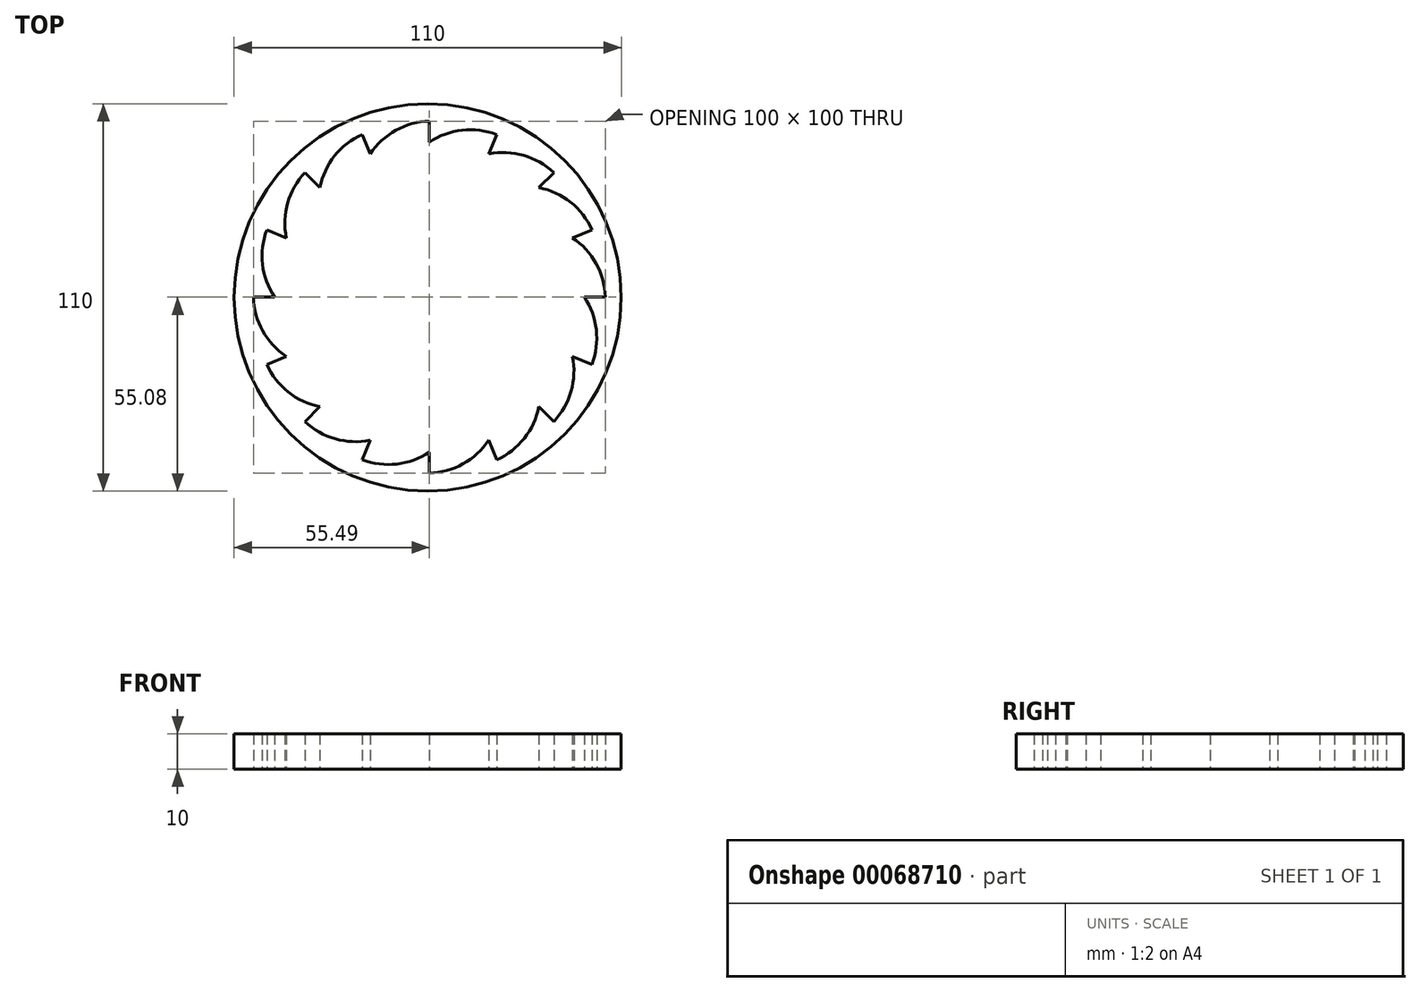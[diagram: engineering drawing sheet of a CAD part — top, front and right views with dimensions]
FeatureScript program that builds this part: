
annotation { "Feature Type Name" : "Feature", "Feature Type Description" : "" }
export const myFeature = defineFeature(function(context is Context, id is Id, definition is map)
    precondition{}
    {
        {
            var Q0;
            Q0=qCreatedBy(makeId("Top.planeOp"),FACE);
            var sketch = newSketch(context, id + "F0", { "sketchPlane" : qUnion([Q0])});
            skLineSegment(sketch, "E0", {"start": v(0, 44) * mm, "end": v(0, 50) * mm});
            skLineSegment(sketch, "E1", {"start": v(16.84, 40.65) * mm, "end": v(19.13, 46.2) * mm});
            skLineSegment(sketch, "E2", {"start": v(35.36, 35.36) * mm, "end": v(31.11, 31.11) * mm});
            skLineSegment(sketch, "E3", {"start": v(40.65, 16.84) * mm, "end": v(46.2, 19.13) * mm});
            skArc(sketch, "E4", {"start": v(19.13, 46.2) * mm, "mid": v(9.3, 47.42) * mm, "end": v(0, 44) * mm});
            skArc(sketch, "E5", {"start": v(35.36, 35.36) * mm, "mid": v(26.74, 40.25) * mm, "end": v(16.84, 40.65) * mm});
            skArc(sketch, "E6", {"start": v(46.2, 19.13) * mm, "mid": v(40.1, 26.95) * mm, "end": v(31.11, 31.11) * mm});
            skArc(sketch, "E7", {"start": v(50, 0) * mm, "mid": v(47.37, 9.55) * mm, "end": v(40.65, 16.84) * mm});
            skLineSegment(sketch, "E8.1.0", {"start": v(-44, 0) * mm, "end": v(-50, 0) * mm});
            skArc(sketch, "E8.1.1", {"start": v(-46.2, 19.13) * mm, "mid": v(-47.42, 9.3) * mm, "end": v(-44, 0) * mm});
            skLineSegment(sketch, "E8.1.2", {"start": v(-40.65, 16.84) * mm, "end": v(-46.2, 19.13) * mm});
            skArc(sketch, "E8.1.3", {"start": v(-35.36, 35.36) * mm, "mid": v(-40.25, 26.74) * mm, "end": v(-40.65, 16.84) * mm});
            skLineSegment(sketch, "E8.1.4", {"start": v(-35.36, 35.36) * mm, "end": v(-31.11, 31.11) * mm});
            skArc(sketch, "E8.1.5", {"start": v(-19.13, 46.2) * mm, "mid": v(-26.95, 40.1) * mm, "end": v(-31.11, 31.11) * mm});
            skArc(sketch, "E8.1.6", {"start": v(0, 50) * mm, "mid": v(-9.55, 47.37) * mm, "end": v(-16.84, 40.65) * mm});
            skLineSegment(sketch, "E8.1.7", {"start": v(-16.84, 40.65) * mm, "end": v(-19.13, 46.2) * mm});
            skLineSegment(sketch, "E8.2.0", {"start": v(0, -44) * mm, "end": v(0, -50) * mm});
            skArc(sketch, "E8.2.1", {"start": v(-19.13, -46.2) * mm, "mid": v(-9.3, -47.42) * mm, "end": v(0, -44) * mm});
            skLineSegment(sketch, "E8.2.2", {"start": v(-16.84, -40.65) * mm, "end": v(-19.13, -46.2) * mm});
            skArc(sketch, "E8.2.3", {"start": v(-35.36, -35.36) * mm, "mid": v(-26.74, -40.25) * mm, "end": v(-16.84, -40.65) * mm});
            skLineSegment(sketch, "E8.2.4", {"start": v(-35.36, -35.36) * mm, "end": v(-31.11, -31.11) * mm});
            skArc(sketch, "E8.2.5", {"start": v(-46.2, -19.13) * mm, "mid": v(-40.1, -26.95) * mm, "end": v(-31.11, -31.11) * mm});
            skArc(sketch, "E8.2.6", {"start": v(-50, 0) * mm, "mid": v(-47.37, -9.55) * mm, "end": v(-40.65, -16.84) * mm});
            skLineSegment(sketch, "E8.2.7", {"start": v(-40.65, -16.84) * mm, "end": v(-46.2, -19.13) * mm});
            skLineSegment(sketch, "E8.3.0", {"start": v(44, 0) * mm, "end": v(50, 0) * mm});
            skArc(sketch, "E8.3.1", {"start": v(46.2, -19.13) * mm, "mid": v(47.42, -9.3) * mm, "end": v(44, 0) * mm});
            skLineSegment(sketch, "E8.3.2", {"start": v(40.65, -16.84) * mm, "end": v(46.2, -19.13) * mm});
            skArc(sketch, "E8.3.3", {"start": v(35.36, -35.36) * mm, "mid": v(40.25, -26.74) * mm, "end": v(40.65, -16.84) * mm});
            skLineSegment(sketch, "E8.3.4", {"start": v(35.36, -35.36) * mm, "end": v(31.11, -31.11) * mm});
            skArc(sketch, "E8.3.5", {"start": v(19.13, -46.2) * mm, "mid": v(26.95, -40.1) * mm, "end": v(31.11, -31.11) * mm});
            skArc(sketch, "E8.3.6", {"start": v(0, -50) * mm, "mid": v(9.55, -47.37) * mm, "end": v(16.84, -40.65) * mm});
            skLineSegment(sketch, "E8.3.7", {"start": v(16.84, -40.65) * mm, "end": v(19.13, -46.2) * mm});
            skPoint(sketch, "E8.center", {"position": v(0, 0) * mm});
            skCircle(sketch, "E9", {"center": v(-0.5, -0.08) * mm, "radius": 55 * mm});
            skSolve(sketch);
        }
        {
            var Q0;
            Q0=makeQuery(id+"F0.imprint","IMPRINT",FACE,{"disambiguationData":[TD([[makeQuery(id+"F0.imprint","IMPRINT",EDGE,{"derivedFrom":sQuery(id+"F0.wireOp",EDGE,"E0")}),-1.0]])]});
            extrude(context, id + "F1", {"entities" : qUnion([Q0]), "depth" : 10 * mm});
        }
    });
